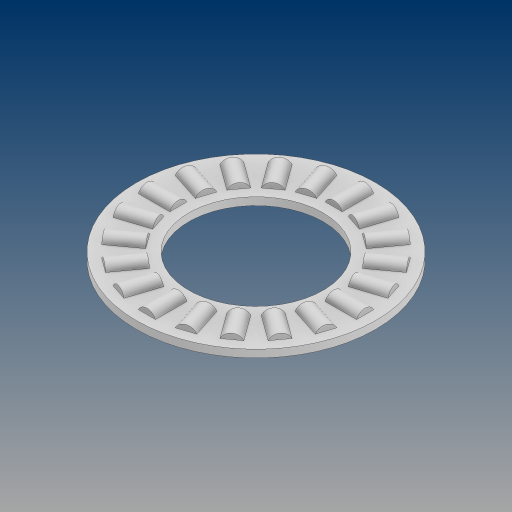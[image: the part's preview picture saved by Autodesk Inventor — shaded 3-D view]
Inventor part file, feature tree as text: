
AUTODESK INVENTOR PART (.ipt)
format: ipt  version: 2024.3 (Build 283343000, 343)  size: 294,912 bytes
history: native  units: in
note: dims shown in document units (in); Inventor stores cm internally (conversion verified against a paired STEP export)
features: other x19, revolve x1, pattern_circular x1
ambient origin geometry x8: Origin, YZ Plane, XZ Plane, XY Plane, X Axis, Y Axis, Z Axis, Center Point
bodies: Solid1 (feature_tree), Solid2 (feature_tree), Solid3 (feature_tree), Solid4 (feature_tree), Solid5 (feature_tree), Solid6 (feature_tree), Solid7 (feature_tree), Solid8 (feature_tree), Solid9 (feature_tree), Solid10 (feature_tree), Solid11 (feature_tree), Solid12 (feature_tree), Solid13 (feature_tree), Solid14 (feature_tree), Solid15 (feature_tree), Solid16 (feature_tree), Solid17 (feature_tree), Solid18 (feature_tree), Solid19 (feature_tree), Solid20 (feature_tree), Solid21 (feature_tree)
feature tree (21):
  revolve  "Revolve2"  [1 undecoded]
  other  "CirPattern1[1]"
  other  "CirPattern1[2]"
  other  "CirPattern1[3]"
  other  "CirPattern1[4]"
  other  "CirPattern1[5]"
  other  "CirPattern1[6]"
  other  "CirPattern1[7]"
  other  "CirPattern1[8]"
  other  "CirPattern1[9]"
  other  "CirPattern1[10]"
  other  "CirPattern1[11]"
  other  "CirPattern1[12]"
  other  "CirPattern1[13]"
  other  "CirPattern1[14]"
  other  "CirPattern1[15]"
  other  "CirPattern1[16]"
  other  "CirPattern1[17]"
  other  "CirPattern1[18]"
  other  "CirPattern1[19]"
  pattern_circular  "CirPattern2"
note: 1 required parameter value undecoded (feature->parameter linkage not recoverable at this tier; creation-order binding heuristic only, values carry confidence <= 0.55)
